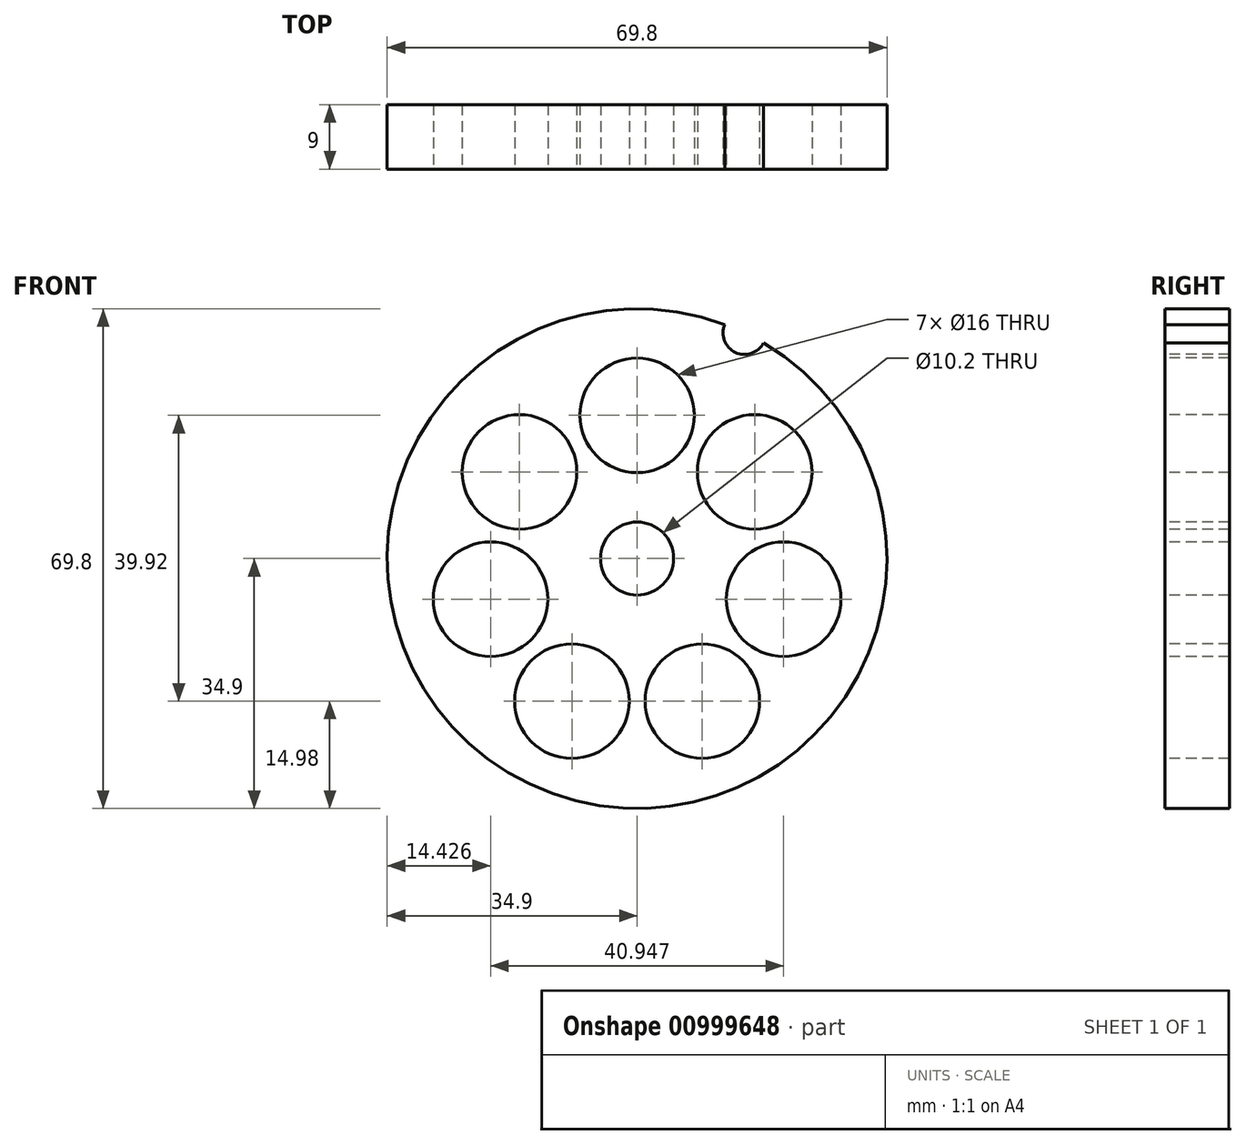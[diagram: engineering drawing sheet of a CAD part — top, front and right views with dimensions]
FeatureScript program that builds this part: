
annotation { "Feature Type Name" : "Feature", "Feature Type Description" : "" }
export const myFeature = defineFeature(function(context is Context, id is Id, definition is map)
    precondition{}
    {
        {
            var Q0;
            Q0=qCreatedBy(makeId("Front.planeOp"),FACE);
            var sketch = newSketch(context, id + "F0", { "sketchPlane" : qUnion([Q0])});
            skCircle(sketch, "E0", {"center": v(0, 0) * mm, "radius": 34.9 * mm});
            skCircle(sketch, "E1", {"center": v(0, 0) * mm, "radius": 5.1 * mm});
            skSolve(sketch);
        }
        {
            var Q0;
            Q0=makeQuery(id+"F0.imprint","IMPRINT",FACE,{"disambiguationData":[TD([[makeQuery(id+"F0.imprint","IMPRINT",EDGE,{"derivedFrom":sQuery(id+"F0.wireOp",EDGE,"E0")}),1.0]])]});
            extrude(context, id + "F1", {"entities" : qUnion([Q0]), "oppositeDirection" : true, "depth" : 9 * mm, "offsetDistance" : 25 * mm});
        }
        {
            var Q0;
            Q0=qCreatedBy(makeId("Front.planeOp"),FACE);
            var sketch = newSketch(context, id + "F2", { "sketchPlane" : qUnion([Q0])});
            skCircle(sketch, "E2", {"center": v(0, 0) * mm, "radius": 30.5 * mm});
            skLineSegment(sketch, "E3", {"start": v(0, 31.4) * mm, "end": v(0, 0) * mm});
            skPoint(sketch, "E4", {"position": v(0, 20) * mm});
            skCircle(sketch, "E5", {"center": v(0, 20) * mm, "radius": 8 * mm});
            skCircle(sketch, "E6.1.0", {"center": v(-16.42, 12.1) * mm, "radius": 8 * mm});
            skCircle(sketch, "E6.2.0", {"center": v(-20.47, -5.67) * mm, "radius": 8 * mm});
            skCircle(sketch, "E6.3.0", {"center": v(-9.11, -19.92) * mm, "radius": 8 * mm});
            skCircle(sketch, "E6.4.0", {"center": v(9.11, -19.92) * mm, "radius": 8 * mm});
            skCircle(sketch, "E6.5.0", {"center": v(20.47, -5.67) * mm, "radius": 8 * mm});
            skPoint(sketch, "E6.center", {"position": v(0, -1) * mm});
            skCircle(sketch, "E7.1.6.0", {"center": v(16.42, 12.1) * mm, "radius": 8 * mm});
            skSolve(sketch);
        }
        {
            var Q0;
            Q0=makeQuery(id+"F2.imprint","IMPRINT",FACE,{"disambiguationData":[TD([[makeQuery(id+"F2.imprint","IMPRINT",EDGE,{"derivedFrom":sQuery(id+"F2.wireOp",EDGE,"E6.6.0")}),1.0]])]});
            var Q1;
            Q1=makeQuery(id+"F2.imprint","IMPRINT",FACE,{"disambiguationData":[TD([[makeQuery(id+"F2.imprint","IMPRINT",EDGE,{"derivedFrom":sQuery(id+"F2.wireOp",EDGE,"E6.1.0")}),1.0]])]});
            var Q2;
            Q2=makeQuery(id+"F2.imprint","IMPRINT",FACE,{"disambiguationData":[TD([[makeQuery(id+"F2.imprint","IMPRINT",EDGE,{"derivedFrom":sQuery(id+"F2.wireOp",EDGE,"E6.2.0")}),1.0]])]});
            var Q3;
            Q3=makeQuery(id+"F2.imprint","IMPRINT",FACE,{"disambiguationData":[TD([[makeQuery(id+"F2.imprint","IMPRINT",EDGE,{"derivedFrom":sQuery(id+"F2.wireOp",EDGE,"E6.3.0")}),1.0]])]});
            var Q4;
            Q4=makeQuery(id+"F2.imprint","IMPRINT",FACE,{"disambiguationData":[TD([[makeQuery(id+"F2.imprint","IMPRINT",EDGE,{"derivedFrom":sQuery(id+"F2.wireOp",EDGE,"E6.4.0")}),1.0]])]});
            var Q5;
            Q5=makeQuery(id+"F2.imprint","IMPRINT",FACE,{"disambiguationData":[TD([[makeQuery(id+"F2.imprint","IMPRINT",EDGE,{"derivedFrom":sQuery(id+"F2.wireOp",EDGE,"E6.5.0")}),1.0]])]});
            var Q6;
            {var subQ0=sQuery(id+"F2.wireOp",EDGE,"E5");var subQ1=sQuery(id+"F2.wireOp",EDGE,"E3");var subQ2=makeQuery(id+"F2.imprint","INTERSECT",VERTEX,{"disambiguationData":[OD(0.0)],"derivedFrom":[subQ1,subQ0]});Q6=makeQuery(id+"F2.imprint","IMPRINT",FACE,{"disambiguationData":[TD([[makeQuery(id+"F2.imprint","IMPRINT",EDGE,{"disambiguationData":[TD([[subQ2,1.0]])],"derivedFrom":subQ1}),1.0]])]});}
            var Q7;
            {var subQ0=sQuery(id+"F2.wireOp",EDGE,"E5");var subQ1=sQuery(id+"F2.wireOp",EDGE,"E3");var subQ2=makeQuery(id+"F2.imprint","INTERSECT",VERTEX,{"disambiguationData":[OD(0.0)],"derivedFrom":[subQ1,subQ0]});Q7=makeQuery(id+"F2.imprint","IMPRINT",FACE,{"disambiguationData":[TD([[makeQuery(id+"F2.imprint","IMPRINT",EDGE,{"disambiguationData":[TD([[subQ2,1.0]])],"derivedFrom":subQ1}),-1.0]])]});}
            var Q8;
            Q8=makeQuery(id+"F2.imprint","IMPRINT",FACE,{"disambiguationData":[TD([[makeQuery(id+"F2.imprint","IMPRINT",EDGE,{"derivedFrom":sQuery(id+"F2.wireOp",EDGE,"E7.1.6.0")}),1.0]])]});
            extrude(context, id + "F3", {"entities" : qUnion([Q0, Q1, Q2, Q3, Q4, Q5, Q6, Q7, Q8]), "operationType" : NewBodyOperationType.REMOVE, "oppositeDirection" : true, "depth" : 10 * mm, "offsetDistance" : 25 * mm});
        }
        {
            var Q0;
            Q0=makeQuery(id+"F1.opExtrude","CAP_FACE",FACE,{"disambiguationData":[OSD([sQuery(id+"F0.wireOp",EDGE,"E0"),sQuery(id+"F0.wireOp",EDGE,"E1")])],"isStart":true});
            var sketch = newSketch(context, id + "F4", { "sketchPlane" : qUnion([Q0])});
            skLineSegment(sketch, "E8", {"start": v(0, 0) * mm, "end": v(15.01, 31.5) * mm});
            skCircle(sketch, "E9", {"center": v(15.01, 31.5) * mm, "radius": 3 * mm});
            skSolve(sketch);
        }
        {
            var Q0;
            {var subQ0=sQuery(id+"F4.wireOp",EDGE,"E8");var subQ1=makeQuery(id+"F1.opExtrude","CAP_EDGE",EDGE,{"disambiguationData":[OSD([sQuery(id+"F0.wireOp",EDGE,"E0")])],"isStart":true});var subQ2=makeQuery(id+"F4.imprint","INTERSECT",VERTEX,{"derivedFrom":[subQ1,subQ0]});Q0=makeQuery(id+"F4.imprint","IMPRINT",FACE,{"disambiguationData":[TD([[makeQuery(id+"F4.imprint","IMPRINT",EDGE,{"disambiguationData":[TD([[subQ2,1.0]])],"derivedFrom":subQ0}),1.0]])]});}
            var Q1;
            {var subQ0=sQuery(id+"F4.wireOp",EDGE,"E8");var subQ1=makeQuery(id+"F1.opExtrude","CAP_EDGE",EDGE,{"disambiguationData":[OSD([sQuery(id+"F0.wireOp",EDGE,"E0")])],"isStart":true});var subQ2=makeQuery(id+"F4.imprint","INTERSECT",VERTEX,{"derivedFrom":[subQ1,subQ0]});Q1=makeQuery(id+"F4.imprint","IMPRINT",FACE,{"disambiguationData":[TD([[makeQuery(id+"F4.imprint","IMPRINT",EDGE,{"disambiguationData":[TD([[subQ2,1.0]])],"derivedFrom":subQ0}),-1.0]])]});}
            extrude(context, id + "F5", {"entities" : qUnion([Q0, Q1]), "operationType" : NewBodyOperationType.REMOVE, "oppositeDirection" : true, "depth" : 10 * mm, "offsetDistance" : 25 * mm});
        }
    });
